# Revit family: Pump_Commercial-Effluent-Zoeller-X6280-X6290_Vertical_Series
name_source: partatom
category: Mechanical Equipment
revit_build: Autodesk Revit 2014 (Build: 20130308_1515(x64)
units: mm (PartAtom-declared; Revit-internal decimal feet)

## types (38) — shared parameters
Assembly Code = D2010900
Bronze Vortex = No
Default Elevation = 0"
Description = Commercial Effluent Pumps for Class I, Division 1, Group C & D Locations
Discharge Diameter = 2"
Discharge Height = 6 5/16"
Discharge Radius = 1"
Height = 25 1/32"
Hertz = 60
Impeller Type = Cast Iron Vortex
Installation Type = Floor Mounted
Length = 13 9/16"
Manufacturer = Zoeller
Material = Cast Iron-Zoeller-Powder Coated Epoxy
Max. Water Temp. = 104 °F
Min. Recommended Fluid Level = 24"
Moisture Detection = Moisture Sensing Probes With Lead Wires
Motor Design Letter = NEMA B
Motor Shaft = 416 S.S.
Motor Type = Submersible
Operation = Non-Automatic
Price = Prices may vary. Please consult Manufacturer Representative for most up-to-date price list.
Product Documentation Link = http://cdn.qleapahead.com
Product Page URL = http://www.zoellerengprod.com
Service Factor = 1.15
Shaft Seal Lower (Options) = Silicon Carbide/Silicon Carbide
Shaft Seal Lower Standard = Silicon Carbide/Carbon
Shaft Seal Upper Standard = Carbon/Ceramic
Shaft Seat Upper (Options) = Carbon/Silicon Carbide, Silicon Carbide/Silicon Carbide
Shipping Weight = 129 lbs (58.5kg)
Solid Size = 2in (50 mm)
Square Ring Seals = Viton
Surface Temperature Code = T5 (1PH) T6 (3PH)
Tandem Seals = Standard
Type = Permanent Split Capacitor or 3 Phase
Type SOW Power Cord Length = 300"
URL = http://www.zoellerengprod.com
Warranty Information = 36 Months (Limited)
Waste Connection = Yes
Width = 10"

## per-type parameters (varying)
| type | Amps | Apparent Load | Flow @ 15 | Flow @ 5' | Insulation | Lead Wires Insulation | Max. Head | Max. Stator Temp. | Model | Motor | Motor Thermal Shutoff | Phase | RPM | Voltage |
| X6282-2"-3" 115V/1Ph/10.3A/0.5HP | 10 A | 1185 VA | 64 GPM | 127 GPM | Class B | Class B | 26' (7.9m) | 266 °F | X6282 | 1/2 HP | Integral Overload With Automatic Reset - 1 Phase | 1 | 1750 | 115 V |
| X6282-2"-3" 200V/1Ph/6.1A/0.5HP | 6 A | 1220 VA | 64 GPM | 127 GPM | Class B | Class B | 26' (7.9m) | 266 °F | X6282 | 1/2 HP | Integral Overload With Automatic Reset - 1 Phase | 1 | 1750 | 200 V |
| X6282-2"-3" 230V/1Ph/5.0A/0.5HP | 5 A | 1150 VA | 64 GPM | 127 GPM | Class B | Class B | 26' (7.9m) | 266 °F | X6282 | 1/2 HP | Integral Overload With Automatic Reset - 1 Phase | 1 | 1750 | 230 V |
| X6282-2"-3" 200V/3Ph/3.6A/0.5HP | 4 A | 720 VA | 64 GPM | 127 GPM | Class B | Class B | 26' (7.9m) | 266 °F | X6282 | 1/2 HP | Thermal Sensor With Lead Wires - 3 Phase | 3 | 1750 | 200 V |
| X6282-2"-3" 230V/3Ph/3.0A/0.5HP | 3 A | 690 VA | 64 GPM | 127 GPM | Class B | Class B | 26' (7.9m) | 266 °F | X6282 | 1/2 HP | Thermal Sensor With Lead Wires - 3 Phase | 3 | 1750 | 230 V |
| X6282-2"-3" 460V/3Ph/1.7A/0.5HP | 2 A | 782 VA | 64 GPM | 127 GPM | Class B | Class B | 26' (7.9m) | 266 °F | X6282 | 1/2 HP | Thermal Sensor With Lead Wires - 3 Phase | 3 | 1750 | 460 V |
| X6282-2"-3" 575V/3Ph/1.4A/0.5HP | 1 A | 805 VA | 64 GPM | 127 GPM | Class B | Class B | 26' (7.9m) | 266 °F | X6282 | 1/2 HP | Thermal Sensor With Lead Wires - 3 Phase | 3 | 1750 | 575 V |
| X6284-2"-3" 200V/1Ph/9.3A/1HP | 9 A | 1860 VA | 133 GPM | 179 GPM | Class B | Class B | 35' (10.7m) | 266 °F | X6284 | 1 HP | Integral Overload With Automatic Reset - 1 Phase | 1 | 1750 | 200 V |
| X6284-2"-3" 230V/1Ph/8.9A/1HP | 9 A | 2047 VA | 133 GPM | 179 GPM | Class B | Class B | 35' (10.7m) | 266 °F | X6284 | 1 HP | Integral Overload With Automatic Reset - 1 Phase | 1 | 1750 | 230 V |
| X6284-2"-3" 200V/3Ph/5.5A/1HP | 6 A | 1100 VA | 133 GPM | 179 GPM | Class B | Class B | 35' (10.7m) | 266 °F | X6284 | 1 HP | Thermal Sensor With Lead Wires - 3 Phase | 3 | 1750 | 200 V |
| X6284-2"-3" 230V/3Ph/5.0A/1HP | 5 A | 1150 VA | 133 GPM | 179 GPM | Class B | Class B | 35' (10.7m) | 266 °F | X6284 | 1 HP | Thermal Sensor With Lead Wires - 3 Phase | 3 | 1750 | 230 V |
| X6284-2"-3" 460V/3Ph/2.6A/1HP | 3 A | 1196 VA | 133 GPM | 179 GPM | Class B | Class B | 35' (10.7m) | 266 °F | X6284 | 1 HP | Thermal Sensor With Lead Wires - 3 Phase | 3 | 1750 | 460 V |
| X6284-2"-3" 575V/3Ph/2.2A/1HP | 2 A | 1265 VA | 133 GPM | 179 GPM | Class B | Class B | 35' (10.7m) | 266 °F | X6284 | 1 HP | Thermal Sensor With Lead Wires - 3 Phase | 3 | 1750 | 575 V |
| X6292-2"-3" 115V/1Ph/15.0A/0.5HP | 15 A | 1725 VA | 104 GPM | 135 GPM | Class B | Class B | 40' (12.2m) | 266 °F | X6292 | 0.5 HP | Integral Overload With Automatic Reset - 1 Phase | 1 | 3450 | 115 V |
| X6292-2"-3" 200V/1Ph/8.8A/0.5HP | 9 A | 1760 VA | 104 GPM | 135 GPM | Class B | Class B | 40' (12.2m) | 266 °F | X6292 | 0.5 HP | Integral Overload With Automatic Reset - 1 Phase | 1 | 3450 | 200 V |
| X6292-2"-3" 230V/1Ph/7.5A/0.5HP | 8 A | 1725 VA | 104 GPM | 135 GPM | Class B | Class B | 40' (12.2m) | 266 °F | X6292 | 0.5 HP | Integral Overload With Automatic Reset - 1 Phase | 1 | 3450 | 230 V |
| X6292-2"-3" 200V/3Ph/6.4A/0.5HP | 6 A | 1280 VA | 104 GPM | 135 GPM | Class B | Class B | 40' (12.2m) | 266 °F | X6292 | 0.5 HP | Thermal Sensor With Lead Wires - 3 Phase | 3 | 3450 | 200 V |
| X6292-2"-3" 230V/3Ph/5.2A/0.5HP | 5 A | 1196 VA | 104 GPM | 135 GPM | Class B | Class B | 40' (12.2m) | 266 °F | X6292 | 0.5 HP | Thermal Sensor With Lead Wires - 3 Phase | 3 | 3450 | 230 V |
| X6292-2"-3" 460V/3Ph/2.9A/0.5HP | 3 A | 1334 VA | 104 GPM | 135 GPM | Class B | Class B | 40' (12.2m) | 266 °F | X6292 | 0.5 HP | Thermal Sensor With Lead Wires - 3 Phase | 3 | 3450 | 460 V |
| X6292-2"-3" 575V/3Ph/2.4A/0.5HP | 2 A | 1380 VA | 104 GPM | 135 GPM | Class B | Class B | 40' (12.2m) | 266 °F | X6292 | 0.5 HP | Thermal Sensor With Lead Wires - 3 Phase | 3 | 3450 | 575 V |
| X6293-2"-3" 200V/1Ph/12.0A/1HP | 12 A | 2400 VA | 122 GPM | 0 GPM | Class B | Class B | 51' (15.5m) | 266 °F | X6293 | 1 HP | Integral Overload With Automatic Reset - 1 Phase | 1 | 3450 | 200 V |
| X6293-2"-3" 230V/1Ph/10.2A/1HP | 10 A | 2346 VA | 122 GPM | 0 GPM | Class B | Class B | 51' (15.5m) | 266 °F | X6293 | 1 HP | Integral Overload With Automatic Reset - 1 Phase | 1 | 3450 | 230 V |
| X6293-2"-3" 200V/3Ph/8.2A/1HP | 8 A | 1640 VA | 122 GPM | 0 GPM | Class B | Class B | 51' (15.5m) | 266 °F | X6293 | 1 HP | Thermal Sensor With Lead Wires - 3 Phase | 3 | 3450 | 200 V |
| X6293-2"-3" 230V/3Ph/7.6A/1HP | 8 A | 1748 VA | 122 GPM | 0 GPM | Class B | Class B | 51' (15.5m) | 266 °F | X6293 | 1 HP | Thermal Sensor With Lead Wires - 3 Phase | 3 | 3450 | 230 V |
| X6293-2"-3" 460V/3Ph/4.0A/1HP | 4 A | 1840 VA | 122 GPM | 0 GPM | Class B | Class B | 51' (15.5m) | 266 °F | X6293 | 1 HP | Thermal Sensor With Lead Wires - 3 Phase | 3 | 3450 | 460 V |
| X6293-2"-3" 575V/3Ph/3.3A/1HP | 3 A | 1898 VA | 122 GPM | 0 GPM | Class B | Class B | 51' (15.5m) | 266 °F | X6293 | 1 HP | Thermal Sensor With Lead Wires - 3 Phase | 3 | 3450 | 575 V |
| X6294-2"-3" 200V/1Ph/17.8A/1.5HP | 18 A | 3560 VA | 165 GPM | 196 GPM | Class F | Class F | 62' (18.9m) | 311 °F | X6294 | 1.5 HP | Integral Overload With Automatic Reset - 1 Phase | 1 | 3450 | 200 V |
| X6294-2"-3" 230V/1Ph/13.7A/1.5HP | 14 A | 3151 VA | 165 GPM | 196 GPM | Class F | Class F | 62' (18.9m) | 311 °F | X6294 | 1.5 HP | Integral Overload With Automatic Reset - 1 Phase | 1 | 3450 | 230 V |
| X6294-2"-3" 200V/3Ph/10.8A/1.5HP | 11 A | 2160 VA | 165 GPM | 196 GPM | Class F | Class F | 62' (18.9m) | 311 °F | X6294 | 1.5 HP | Thermal Sensor With Lead Wires - 3 Phase | 3 | 3450 | 200 V |
| X6294-2"-3" 230V/3Ph/9.5A/1.5HP | 10 A | 2185 VA | 165 GPM | 196 GPM | Class F | Class F | 62' (18.9m) | 311 °F | X6294 | 1.5 HP | Thermal Sensor With Lead Wires - 3 Phase | 3 | 3450 | 230 V |
| X6294-2"-3" 460V/3Ph/4.8A/1.5HP | 5 A | 2208 VA | 165 GPM | 196 GPM | Class F | Class F | 62' (18.9m) | 311 °F | X6294 | 1.5 HP | Thermal Sensor With Lead Wires - 3 Phase | 3 | 3450 | 460 V |
| X6294-2"-3" 575V/3Ph/3.8A/1.5HP | 4 A | 2185 VA | 165 GPM | 196 GPM | Class F | Class F | 62' (18.9m) | 311 °F | X6294 | 1.5 HP | Thermal Sensor With Lead Wires - 3 Phase | 3 | 3450 | 575 V |
| X6295-2"-3" 200V/1Ph/20.5A/2HP | 21 A | 4100 VA | 186 GPM | 214 GPM | Class F | Class F | 75' (22.9m) | 311 °F | X6295 | 2 HP | Integral Overload With Automatic Reset - 1 Phase | 1 | 3450 | 200 V |
| X6295-2"-3" 230V/1Ph/17.1A/2HP | 17 A | 3933 VA | 186 GPM | 214 GPM | Class F | Class F | 75' (22.9m) | 311 °F | X6295 | 2 HP | Integral Overload With Automatic Reset - 1 Phase | 1 | 3450 | 230 V |
| X6295-2"-3" 200V/3Ph/14.3A/2HP | 14 A | 2860 VA | 186 GPM | 214 GPM | Class F | Class F | 75' (22.9m) | 311 °F | X6295 | 2 HP | Thermal Sensor With Lead Wires - 3 Phase | 3 | 3450 | 200 V |
| X6295-2"-3" 230V/3Ph/12.2A/2HP | 12 A | 2806 VA | 186 GPM | 214 GPM | Class F | Class F | 75' (22.9m) | 311 °F | X6295 | 2 HP | Thermal Sensor With Lead Wires - 3 Phase | 3 | 3450 | 230 V |
| X6295-2"-3" 460V/3Ph/6.1A/2HP | 6 A | 2806 VA | 186 GPM | 214 GPM | Class F | Class F | 75' (22.9m) | 311 °F | X6295 | 2 HP | Thermal Sensor With Lead Wires - 3 Phase | 3 | 3450 | 460 V |
| X6295-2"-3" 575V/3Ph/4.9A/2HP | 5 A | 2818 VA | 186 GPM | 214 GPM | Class F | Class F | 75' (22.9m) | 311 °F | X6295 | 2 HP | Thermal Sensor With Lead Wires - 3 Phase | 3 | 3450 | 575 V |

## geometry (parser evidence)
native form markers: Sweep x2
no freeform markers — native parametric forms only
